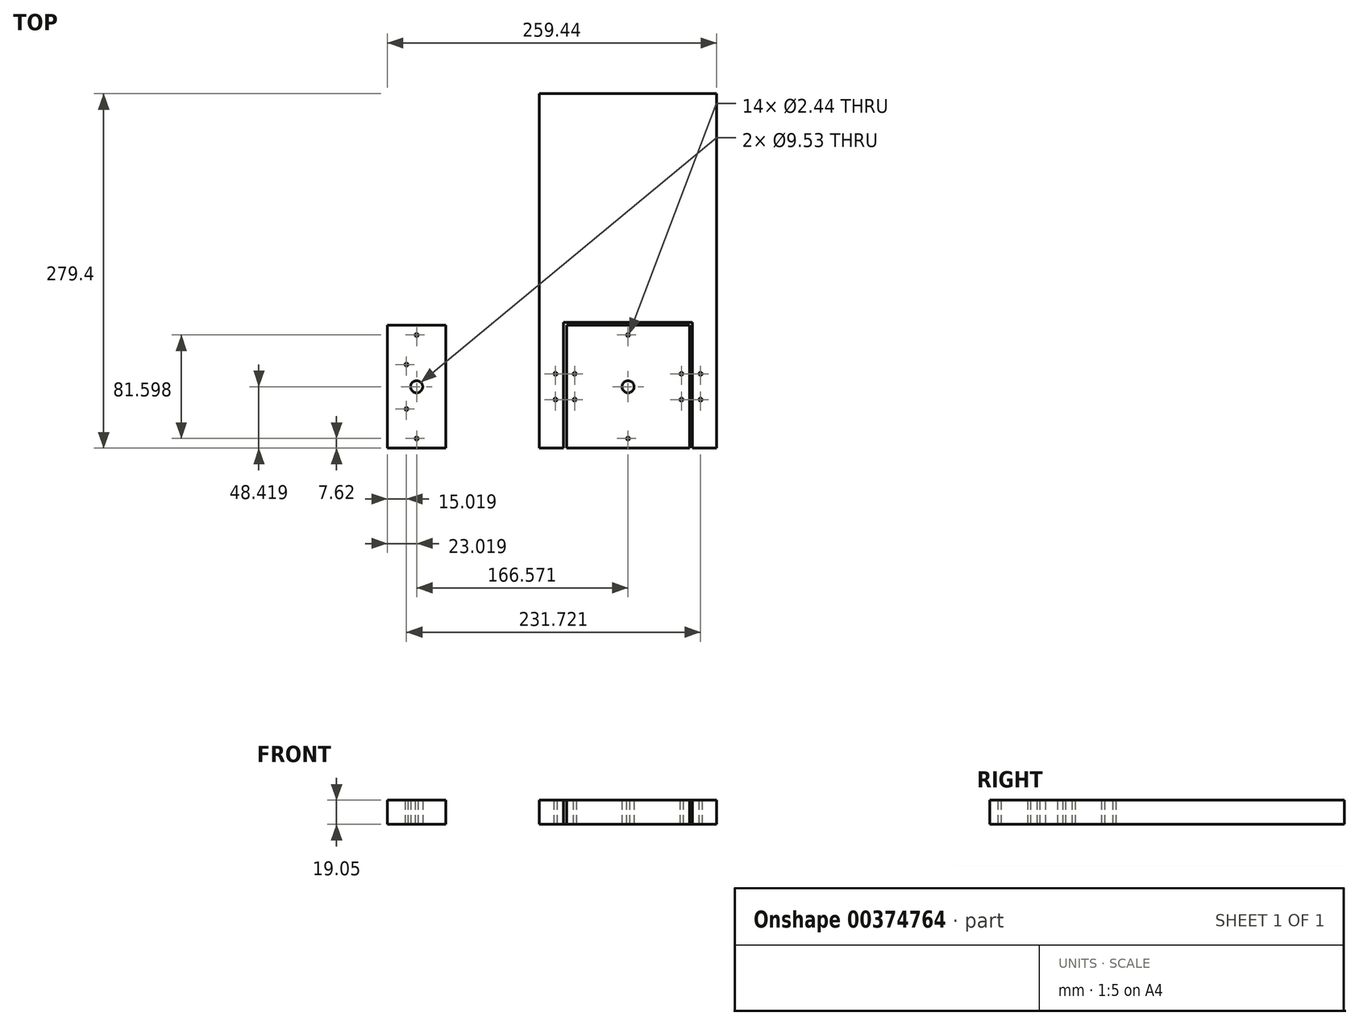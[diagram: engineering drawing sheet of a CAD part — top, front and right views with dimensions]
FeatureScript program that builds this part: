
annotation { "Feature Type Name" : "Feature", "Feature Type Description" : "" }
export const myFeature = defineFeature(function(context is Context, id is Id, definition is map)
    precondition{}
    {
        {
            var Q0;
            Q0=qCreatedBy(makeId("Top.planeOp"),FACE);
            var sketch = newSketch(context, id + "F0", { "sketchPlane" : qUnion([Q0])});
            skLineSegment(sketch, "E0.bottom", {"start": v(69.85, -139.7) * mm, "end": v(50.8, -139.7) * mm});
            skLineSegment(sketch, "E0.top", {"start": v(69.85, 139.7) * mm, "end": v(-69.85, 139.7) * mm});
            skLineSegment(sketch, "E0.left", {"start": v(69.85, -139.7) * mm, "end": v(69.85, 139.7) * mm});
            skLineSegment(sketch, "E0.right", {"start": v(-69.85, -139.7) * mm, "end": v(-69.85, 139.7) * mm});
            skPoint(sketch, "E0.middle", {"position": v(0, 0) * mm});
            skLineSegment(sketch, "E1", {"start": v(-50.8, -139.7) * mm, "end": v(-69.85, -139.7) * mm});
            skLineSegment(sketch, "E2", {"start": v(50.8, -40.48) * mm, "end": v(-50.8, -40.48) * mm});
            skLineSegment(sketch, "E3", {"start": v(-50.8, -40.48) * mm, "end": v(-50.8, -139.7) * mm});
            skLineSegment(sketch, "E4", {"start": v(50.8, -40.48) * mm, "end": v(50.8, -139.7) * mm});
            skLineSegment(sketch, "E5.bottom", {"start": v(-48.42, -139.7) * mm, "end": v(48.42, -139.7) * mm});
            skLineSegment(sketch, "E5.top", {"start": v(-48.42, -42.86) * mm, "end": v(48.42, -42.86) * mm});
            skLineSegment(sketch, "E5.left", {"start": v(-48.42, -139.7) * mm, "end": v(-48.42, -42.86) * mm});
            skLineSegment(sketch, "E5.right", {"start": v(48.42, -139.7) * mm, "end": v(48.42, -42.86) * mm});
            skLineSegment(sketch, "E6.bottom", {"start": v(114.2, -72.23) * mm, "end": v(101.5, -72.23) * mm});
            skLineSegment(sketch, "E6.top", {"start": v(114.2, -110.33) * mm, "end": v(101.5, -110.33) * mm});
            skLineSegment(sketch, "E6.left", {"start": v(114.2, -72.23) * mm, "end": v(114.2, -110.33) * mm});
            skLineSegment(sketch, "E6.right", {"start": v(101.5, -72.23) * mm, "end": v(101.5, -110.33) * mm});
            skLineSegment(sketch, "E7", {"start": v(-48.42, -139.7) * mm, "end": v(48.42, -42.86) * mm});
            skPoint(sketch, "E8", {"position": v(0, -91.28) * mm});
            skLineSegment(sketch, "E9", {"start": v(101.5, -110.33) * mm, "end": v(114.2, -72.23) * mm});
            skPoint(sketch, "E10", {"position": v(107.84, -91.28) * mm});
            skPoint(sketch, "E11", {"position": v(107.84, -81.12) * mm});
            skPoint(sketch, "E12", {"position": v(107.84, -101.44) * mm});
            skPoint(sketch, "E13", {"position": v(57.15, -81.12) * mm});
            skPoint(sketch, "E14", {"position": v(42.07, -81.12) * mm});
            skPoint(sketch, "E15", {"position": v(57.15, -101.44) * mm});
            skPoint(sketch, "E16", {"position": v(42.07, -101.44) * mm});
            skPoint(sketch, "E17", {"position": v(-42.07, -81.12) * mm});
            skPoint(sketch, "E18", {"position": v(-57.15, -81.12) * mm});
            skPoint(sketch, "E19", {"position": v(-57.15, -101.44) * mm});
            skPoint(sketch, "E20", {"position": v(-42.07, -101.44) * mm});
            skCircle(sketch, "E21", {"center": v(-174.57, -91.28) * mm, "radius": 14 * mm});
            skPoint(sketch, "E22", {"position": v(-174.57, -108.78) * mm});
            skPoint(sketch, "E23", {"position": v(-174.57, -73.78) * mm});
            skPoint(sketch, "E24", {"position": v(-166.57, -91.28) * mm});
            skPoint(sketch, "E25", {"position": v(0, -50.48) * mm});
            skPoint(sketch, "E26", {"position": v(0, -132.08) * mm});
            skLineSegment(sketch, "E27.bottom", {"start": v(-143.55, -42.86) * mm, "end": v(-189.6, -42.86) * mm});
            skLineSegment(sketch, "E27.top", {"start": v(-143.55, -139.7) * mm, "end": v(-189.6, -139.7) * mm});
            skLineSegment(sketch, "E27.left", {"start": v(-143.55, -42.86) * mm, "end": v(-143.55, -139.7) * mm});
            skLineSegment(sketch, "E27.right", {"start": v(-189.6, -42.86) * mm, "end": v(-189.6, -61.91) * mm});
            skLineSegment(sketch, "E28", {"start": v(-189.6, -139.7) * mm, "end": v(-143.55, -42.86) * mm});
            skPoint(sketch, "E29", {"position": v(-166.57, -50.48) * mm});
            skPoint(sketch, "E30", {"position": v(-166.57, -132.08) * mm});
            skLineSegment(sketch, "E31.bottom", {"start": v(-118.15, -143.82) * mm, "end": v(-215, -143.82) * mm});
            skLineSegment(sketch, "E31.top", {"start": v(-118.15, -158.57) * mm, "end": v(-215, -158.57) * mm});
            skLineSegment(sketch, "E31.left", {"start": v(-118.15, -143.82) * mm, "end": v(-118.15, -158.57) * mm});
            skLineSegment(sketch, "E31.right", {"start": v(-215, -143.82) * mm, "end": v(-215, -158.57) * mm});
            skLineSegment(sketch, "E32", {"start": v(-215, -158.57) * mm, "end": v(-118.15, -143.82) * mm});
            skPoint(sketch, "E33", {"position": v(-166.57, -151.2) * mm});
            skLineSegment(sketch, "E34", {"start": v(-189.6, -61.91) * mm, "end": v(-189.6, -120.65) * mm});
            skLineSegment(sketch, "E35", {"start": v(-189.6, -120.65) * mm, "end": v(-189.6, -139.7) * mm});
            skLineSegment(sketch, "E36.right", {"start": v(-143.55, -61.91) * mm, "end": v(-143.55, -83.21) * mm});
            skSolve(sketch);
        }
        {
            var Q0;
            Q0=makeQuery(id+"F0.imprint","IMPRINT",FACE,{"disambiguationData":[TD([[makeQuery(id+"F0.imprint","IMPRINT",EDGE,{"derivedFrom":sQuery(id+"F0.wireOp",EDGE,"E0.bottom")}),-1.0]])]});
            var Q1;
            Q1=makeQuery(id+"F0.imprint","IMPRINT",FACE,{"disambiguationData":[TD([[makeQuery(id+"F0.imprint","IMPRINT",EDGE,{"derivedFrom":sQuery(id+"F0.wireOp",EDGE,"E5.bottom")}),1.0]])]});
            var Q2;
            Q2=makeQuery(id+"F0.imprint","IMPRINT",FACE,{"disambiguationData":[TD([[makeQuery(id+"F0.imprint","IMPRINT",EDGE,{"derivedFrom":sQuery(id+"F0.wireOp",EDGE,"E5.top")}),-1.0]])]});
            var Q3;
            {var subQ0=sQuery(id+"F0.wireOp",EDGE,"E21");var subQ1=sQuery(id+"F0.wireOp",EDGE,"E7");var subQ2=makeQuery(id+"F0.imprint","INTERSECT",VERTEX,{"disambiguationData":[OD(0.0)],"derivedFrom":[subQ1,subQ0]});Q3=makeQuery(id+"F0.imprint","IMPRINT",FACE,{"disambiguationData":[TD([[makeQuery(id+"F0.imprint","IMPRINT",EDGE,{"disambiguationData":[TD([[subQ2,-1.0]])],"derivedFrom":subQ1}),1.0]])]});}
            var Q4;
            {var subQ0=sQuery(id+"F0.wireOp",EDGE,"E21");var subQ1=sQuery(id+"F0.wireOp",EDGE,"E7");var subQ2=makeQuery(id+"F0.imprint","INTERSECT",VERTEX,{"disambiguationData":[OD(0.0)],"derivedFrom":[subQ1,subQ0]});Q4=makeQuery(id+"F0.imprint","IMPRINT",FACE,{"disambiguationData":[TD([[makeQuery(id+"F0.imprint","IMPRINT",EDGE,{"disambiguationData":[TD([[subQ2,-1.0]])],"derivedFrom":subQ1}),-1.0]])]});}
            extrude(context, id + "F1", {"entities" : qUnion([Q0, Q1, Q2, Q3, Q4]), "depth" : 19.05 * mm});
        }
        {
            var Q0;
            Q0=sQuery(id+"F0.wireOp",VERTEX,"E18");
            var Q1;
            Q1=sQuery(id+"F0.wireOp",VERTEX,"E19");
            var Q2;
            Q2=sQuery(id+"F0.wireOp",VERTEX,"E20");
            var Q3;
            Q3=sQuery(id+"F0.wireOp",VERTEX,"E17");
            var Q4;
            Q4=sQuery(id+"F0.wireOp",VERTEX,"E14");
            var Q5;
            Q5=sQuery(id+"F0.wireOp",VERTEX,"E13");
            var Q6;
            Q6=sQuery(id+"F0.wireOp",VERTEX,"E15");
            var Q7;
            Q7=sQuery(id+"F0.wireOp",VERTEX,"E16");
            var Q8;
            Q8=sQuery(id+"F0.wireOp",VERTEX,"E25");
            var Q9;
            Q9=sQuery(id+"F0.wireOp",VERTEX,"E26");
            var Q10;
            Q10=makeQuery(id+"F1.opExtrude","SWEPT_BODY",BODY,{"disambiguationData":[OSD([sQuery(id+"F0.wireOp",EDGE,"E0.bottom"),sQuery(id+"F0.wireOp",EDGE,"E0.top"),sQuery(id+"F0.wireOp",EDGE,"E0.left"),sQuery(id+"F0.wireOp",EDGE,"E0.right"),sQuery(id+"F0.wireOp",EDGE,"E1"),sQuery(id+"F0.wireOp",EDGE,"E2"),sQuery(id+"F0.wireOp",EDGE,"E3"),sQuery(id+"F0.wireOp",EDGE,"E4")])]});
            var Q11;
            Q11=makeQuery(id+"F1.opExtrude","SWEPT_BODY",BODY,{"disambiguationData":[OSD([sQuery(id+"F0.wireOp",EDGE,"E5.bottom"),sQuery(id+"F0.wireOp",EDGE,"E5.top"),sQuery(id+"F0.wireOp",EDGE,"E5.left"),sQuery(id+"F0.wireOp",EDGE,"E5.right")])]});
            hole(context, id + "F2", {"style" : HoleStyle.SIMPLE, "endStyle" : HoleEndStyle.THROUGH, "oppositeDirection" : true, "standardTappedOrClearance" : lookupTablePath({ "standard" : "ANSI", "fit" : "Normal (ASME)", "size" : "#2", "type" : "Clearance" }), "standardBlindInLast" : lookupTablePath({ "fit" : "Free", "standard" : "ANSI", "size" : "#2", "type" : "Clearance" }), "holeDiameter" : 2.44 * mm, "isTappedThrough" : true, "tappedDepth" : 12.7 * mm, "tapClearance" : 3, "locations" : qUnion([Q0, Q1, Q2, Q3, Q4, Q5, Q6, Q7, Q8, Q9]), "scope" : qUnion([Q10, Q11])});
        }
        {
            var Q0;
            Q0=makeQuery(id+"F0.imprint","IMPRINT",FACE,{"disambiguationData":[TD([[makeQuery(id+"F0.imprint","IMPRINT",EDGE,{"derivedFrom":sQuery(id+"F0.wireOp",EDGE,"E27.bottom")}),1.0]])]});
            var Q1;
            Q1=makeQuery(id+"F0.imprint","IMPRINT",FACE,{"disambiguationData":[TD([[makeQuery(id+"F0.imprint","IMPRINT",EDGE,{"derivedFrom":sQuery(id+"F0.wireOp",EDGE,"E27.top")}),-1.0]])]});
            var Q2;
            {var subQ0=sQuery(id+"F0.wireOp",EDGE,"E27.right");var subQ1=sQuery(id+"F0.wireOp",EDGE,"E21");var subQ2=makeQuery(id+"F0.imprint","INTERSECT",VERTEX,{"disambiguationData":[OD(0.0)],"derivedFrom":[subQ1,subQ0]});Q2=makeQuery(id+"F0.imprint","IMPRINT",FACE,{"disambiguationData":[TD([[makeQuery(id+"F0.imprint","IMPRINT",EDGE,{"disambiguationData":[TD([[subQ2,-1.0]])],"derivedFrom":subQ1}),-1.0]])]});}
            var Q3;
            {var subQ5=sQuery(id+"F0.wireOp",EDGE,"CLbaFe1l-RwgK-LAMh-LH5Y-tR9eX3XhQKco.bottom");Q3=makeQuery(id+"F0.imprint","IMPRINT",FACE,{"disambiguationData":[TD([[makeQuery(id+"F0.imprint","IMPRINT",EDGE,{"derivedFrom":subQ5}),1.0]])]});}
            var Q4;
            {var subQ0=sQuery(id+"F0.wireOp",EDGE,"E35");var subQ1=sQuery(id+"F0.wireOp",EDGE,"E21");var subQ2=makeQuery(id+"F0.imprint","INTERSECT",VERTEX,{"derivedFrom":[subQ1,subQ0]});Q4=makeQuery(id+"F0.imprint","IMPRINT",FACE,{"disambiguationData":[TD([[makeQuery(id+"F0.imprint","IMPRINT",EDGE,{"disambiguationData":[TD([[subQ2,-1.0]])],"derivedFrom":subQ1}),-1.0]])]});}
            var Q5;
            {var subQ0=sQuery(id+"F0.wireOp",EDGE,"E28");var subQ1=sQuery(id+"F0.wireOp",EDGE,"E21");var subQ2=makeQuery(id+"F0.imprint","INTERSECT",VERTEX,{"disambiguationData":[OD(0.0)],"derivedFrom":[subQ1,subQ0]});Q5=makeQuery(id+"F0.imprint","IMPRINT",FACE,{"disambiguationData":[TD([[makeQuery(id+"F0.imprint","IMPRINT",EDGE,{"disambiguationData":[TD([[subQ2,-1.0]])],"derivedFrom":subQ1}),1.0]])]});}
            var Q6;
            {var subQ0=sQuery(id+"F0.wireOp",EDGE,"E28");var subQ1=sQuery(id+"F0.wireOp",EDGE,"E21");var subQ2=makeQuery(id+"F0.imprint","INTERSECT",VERTEX,{"disambiguationData":[OD(0.0)],"derivedFrom":[subQ1,subQ0]});Q6=makeQuery(id+"F0.imprint","IMPRINT",FACE,{"disambiguationData":[TD([[makeQuery(id+"F0.imprint","IMPRINT",EDGE,{"disambiguationData":[TD([[subQ2,1.0]])],"derivedFrom":subQ1}),1.0]])]});}
            extrude(context, id + "F3", {"entities" : qUnion([Q0, Q1, Q2, Q3, Q4, Q5, Q6]), "depth" : 19.05 * mm});
        }
        {
            var Q0;
            Q0=sQuery(id+"F0.wireOp",VERTEX,"E24");
            var Q1;
            Q1=sQuery(id+"F0.wireOp",VERTEX,"E8");
            var Q2;
            Q2=makeQuery(id+"F1.opExtrude","SWEPT_BODY",BODY,{"disambiguationData":[OSD([sQuery(id+"F0.wireOp",EDGE,"E5.bottom"),sQuery(id+"F0.wireOp",EDGE,"E5.top"),sQuery(id+"F0.wireOp",EDGE,"E5.left"),sQuery(id+"F0.wireOp",EDGE,"E5.right")])]});
            var Q3;
            Q3=makeQuery(id+"F3.opExtrude","SWEPT_BODY",BODY,{"disambiguationData":[OSD([sQuery(id+"F0.wireOp",EDGE,"E27.bottom"),sQuery(id+"F0.wireOp",EDGE,"E27.top"),sQuery(id+"F0.wireOp",EDGE,"E27.left"),sQuery(id+"F0.wireOp",EDGE,"E27.right")])]});
            hole(context, id + "F4", {"style" : HoleStyle.SIMPLE, "endStyle" : HoleEndStyle.THROUGH, "oppositeDirection" : true, "holeDiameter" : 9.52 * mm, "isTappedThrough" : true, "tappedDepth" : 12.7 * mm, "tapClearance" : 3, "locations" : qUnion([Q0, Q1]), "scope" : qUnion([Q2, Q3])});
        }
        {
            var Q0;
            Q0=sQuery(id+"F0.wireOp",VERTEX,"E29");
            var Q1;
            Q1=sQuery(id+"F0.wireOp",VERTEX,"E23");
            var Q2;
            Q2=sQuery(id+"F0.wireOp",VERTEX,"E22");
            var Q3;
            Q3=sQuery(id+"F0.wireOp",VERTEX,"E30");
            var Q4;
            Q4=makeQuery(id+"F3.opExtrude","SWEPT_BODY",BODY,{"disambiguationData":[OSD([sQuery(id+"F0.wireOp",EDGE,"E27.bottom"),sQuery(id+"F0.wireOp",EDGE,"E27.top"),sQuery(id+"F0.wireOp",EDGE,"E27.left"),sQuery(id+"F0.wireOp",EDGE,"E27.right")])]});
            hole(context, id + "F5", {"style" : HoleStyle.SIMPLE, "endStyle" : HoleEndStyle.THROUGH, "oppositeDirection" : true, "standardTappedOrClearance" : lookupTablePath({ "standard" : "ANSI", "fit" : "Normal (ASME)", "size" : "#2", "type" : "Clearance" }), "standardBlindInLast" : lookupTablePath({ "fit" : "Free", "standard" : "ANSI", "size" : "#2", "type" : "Clearance" }), "holeDiameter" : 2.44 * mm, "isTappedThrough" : true, "tappedDepth" : 12.7 * mm, "tapClearance" : 3, "locations" : qUnion([Q0, Q1, Q2, Q3]), "scope" : qUnion([Q4])});
        }
    });
